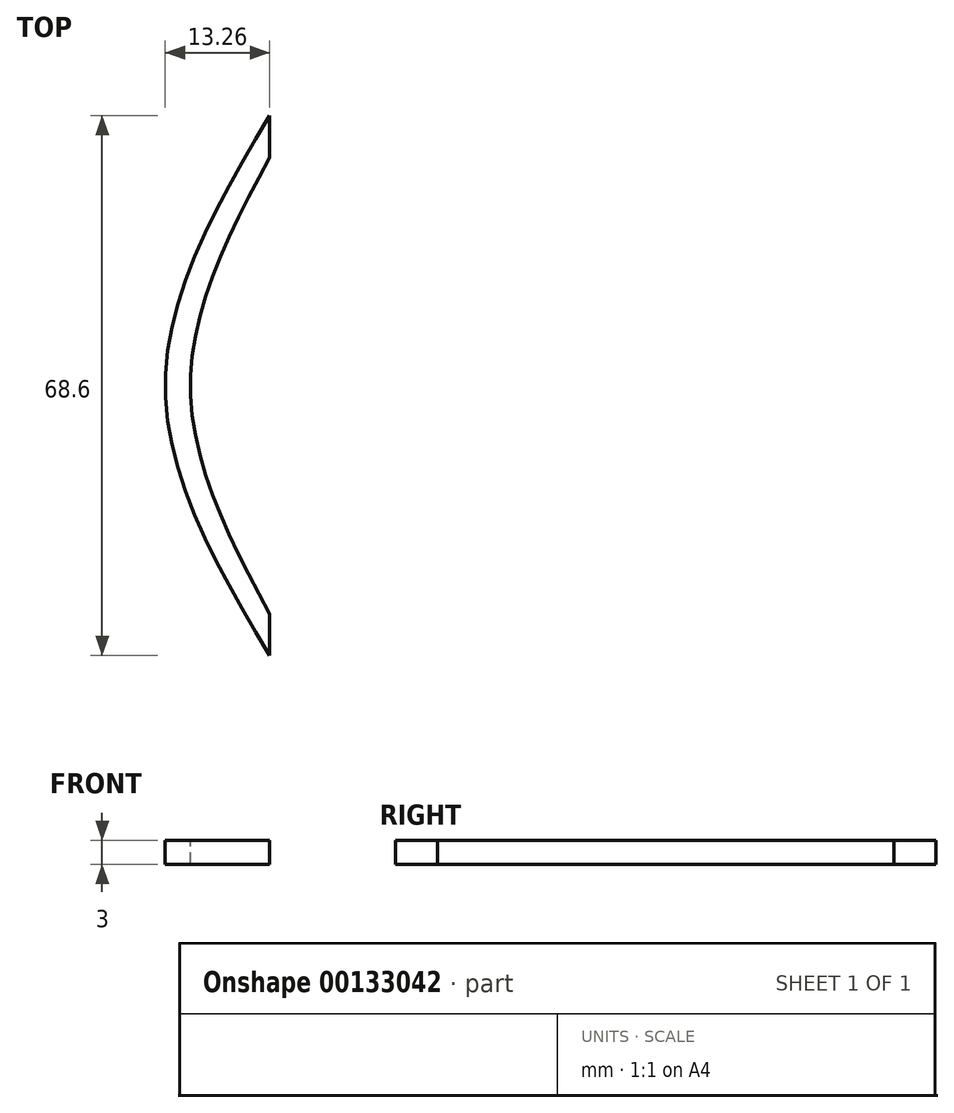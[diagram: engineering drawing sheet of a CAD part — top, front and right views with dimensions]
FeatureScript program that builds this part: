
annotation { "Feature Type Name" : "Feature", "Feature Type Description" : "" }
export const myFeature = defineFeature(function(context is Context, id is Id, definition is map)
    precondition{}
    {
        {
            var Q0;
            Q0=qCreatedBy(makeId("Top.planeOp"),FACE);
            var sketch = newSketch(context, id + "F0", { "sketchPlane" : qUnion([Q0])});
            skLineSegment(sketch, "E0", {"start": v(-31, 0) * mm, "end": v(-43, 0) * mm, "construction": true});
            skLineSegment(sketch, "E1", {"start": v(-31, 20) * mm, "end": v(-43, 20) * mm, "construction": true});
            skLineSegment(sketch, "E2", {"start": v(-43, 20) * mm, "end": v(-43, -20) * mm, "construction": true});
            skLineSegment(sketch, "E3", {"start": v(-43, 0) * mm, "end": v(-46.2, 0) * mm, "construction": true});
            skFitSpline(sketch, "E4", {"points": [v(-31, 37.5) * mm, v(-46.2, 0) * mm, v(-31, -37.5) * mm], "startDerivative": vector(-45.6, -75) * mm, "endDerivative": vector(45.6, -75) * mm});
            skFitSpline(sketch, "E5", {"points": [v(-31, 32.5) * mm, v(-43, 0) * mm, v(-31, -32.5) * mm], "startDerivative": vector(-36, -65) * mm, "endDerivative": vector(36, -65) * mm});
            skLineSegment(sketch, "E6", {"start": v(-32.94, 34.3) * mm, "end": v(-32.94, 28.98) * mm});
            skLineSegment(sketch, "E7.MirrorCS", {"start": v(-32.94, -34.3) * mm, "end": v(-32.94, -28.98) * mm});
            skPoint(sketch, "E8.end.orphan", {"position": v(-31, -20) * mm});
            skPoint(sketch, "E9.orphan", {"position": v(-31, -7.5) * mm});
            skPoint(sketch, "E10.start.orphan", {"position": v(-31, 7.5) * mm});
            skPoint(sketch, "E11.end.orphan", {"position": v(-31, 34.3) * mm});
            skSolve(sketch);
        }
        {
            var Q0;
            Q0=qSketchRegion(id+"F0",true);
            extrude(context, id + "F1", {"entities" : qUnion([Q0]), "endBound" : BoundingType.SYMMETRIC, "depth" : 3 * mm});
        }
    });
